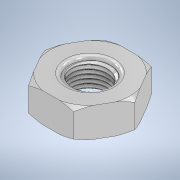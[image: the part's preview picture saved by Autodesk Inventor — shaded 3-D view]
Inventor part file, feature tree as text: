
AUTODESK INVENTOR PART (.ipt)
format: ipt  version: 2020 (Build 240168000, 168)  size: 713,728 bytes
history: native  units: in
note: dims shown in document units (in); Inventor stores cm internally (conversion verified against a paired STEP export)
features: sketch x4, fillet x2, revolve x2, extrude x1, hole x1, thread x1, helix x1, plane x1, projected_geometry x1
ambient origin geometry x8: Origin, YZ Plane, XZ Plane, XY Plane, X Axis, Y Axis, Z Axis, Center Point
bodies: Solid1 (feature_tree), Solid2 (feature_tree)
feature tree (14):
  sketch  "Sketch1"  dims[d0=1.063in d1=0.403in d2=0.0in]
  extrude  "Extrusion1"  Depth=0.403in TaperAngle=0.0deg
  hole  "Hole1"  [1 undecoded]
  fillet  "Fillet1"  Radius=0.05in
  fillet  "Fillet2"  Radius=0.303in
  thread  "Thread1"  [1 undecoded]
  revolve  "Revolution1"  [1 undecoded]
  helix  "Coil1"  [1 undecoded]
  plane  "Work Plane1"
  revolve  "Revolution2"  Angle=60.0deg
  sketch  "Sketch2"  dims[d3=0.565in d4=1.25in d5=0.375in d6=0.25in d7=0.5635in d8=1.528in d9=0.0in d10=0.05in d11=0.05in d12=0.303in d13=0.0in d14=0.3779in d15=0.0089in d16=0.0089in]
  sketch  "Sketch3"  dims[d19=0.0556in d21=0.3779in d23=0.0in]
  sketch  "Sketch5"  dims[d24=0.0556in d25=0.4141in d26=0.3937in d27=0.0in d28=0.0in d29=0.0in d30=0.0in d31=0.0in d34=60.0deg d35=0.04in d36=90.0deg]
  projected_geometry  "Projected Loop2"
note: 4 required parameter values undecoded (feature->parameter linkage not recoverable at this tier; creation-order binding heuristic only, values carry confidence <= 0.55)